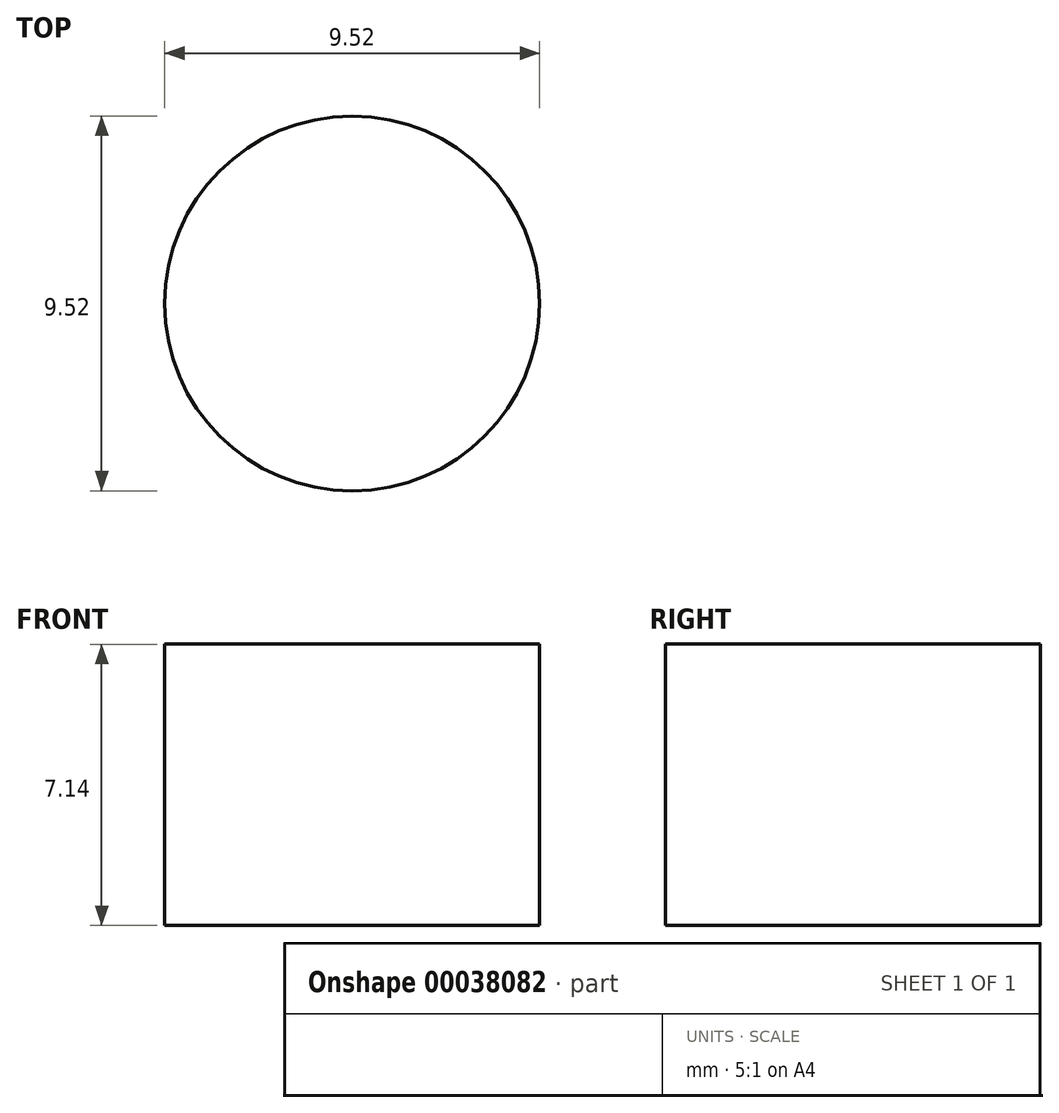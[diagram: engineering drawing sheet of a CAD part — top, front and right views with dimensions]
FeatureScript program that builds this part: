
annotation { "Feature Type Name" : "Feature", "Feature Type Description" : "" }
export const myFeature = defineFeature(function(context is Context, id is Id, definition is map)
    precondition{}
    {
        {
            var Q0;
            Q0=qCreatedBy(makeId("Top.planeOp"),FACE);
            var sketch = newSketch(context, id + "F0", { "sketchPlane" : qUnion([Q0])});
            skCircle(sketch, "E0", {"center": v(0, 0) * mm, "radius": 4.76 * mm});
            skSolve(sketch);
        }
        {
            var Q0;
            Q0=qSketchRegion(id+"F0",true);
            extrude(context, id + "F1", {"entities" : qUnion([Q0]), "depth" : 7.14 * mm});
        }
    });
